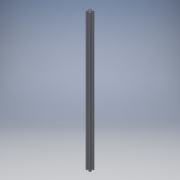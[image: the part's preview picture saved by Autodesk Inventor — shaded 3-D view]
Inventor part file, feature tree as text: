
AUTODESK INVENTOR PART (.ipt)
format: ipt  version: 2019 (Build 230136000, 136)  size: 144,896 bytes
history: native  units: mm
features: other x1, extrude x1, sketch x1
ambient origin geometry x8: Origin, YZ Plane, XZ Plane, XY Plane, X Axis, Y Axis, Z Axis, Center Point
bodies: Body1 (feature_tree)
feature tree (3):
  other  "솔리드1"
  extrude  "돌출1"  Depth=600.0mm TaperAngle=0.0deg
  sketch  "스케치1"
